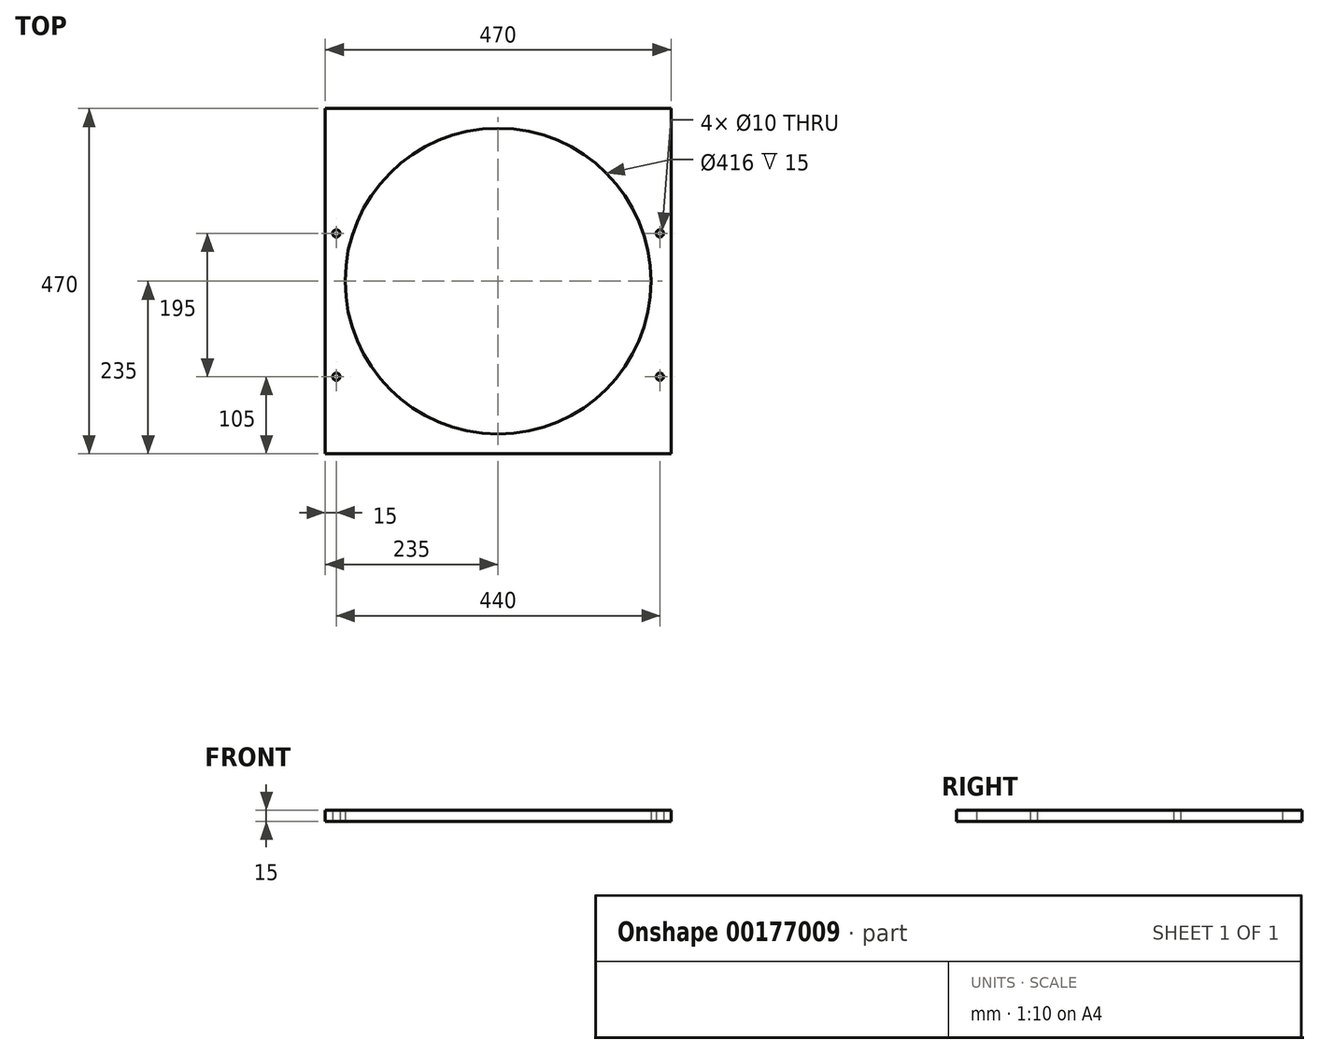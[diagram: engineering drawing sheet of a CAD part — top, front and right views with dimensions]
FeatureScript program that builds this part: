
annotation { "Feature Type Name" : "Feature", "Feature Type Description" : "" }
export const myFeature = defineFeature(function(context is Context, id is Id, definition is map)
    precondition{}
    {
        {
            var Q0;
            Q0=qCreatedBy(makeId("Top.planeOp"),FACE);
            var sketch = newSketch(context, id + "F0", { "sketchPlane" : qUnion([Q0])});
            skLineSegment(sketch, "E0.bottom", {"start": v(-235, 235) * mm, "end": v(235, 235) * mm});
            skLineSegment(sketch, "E0.top", {"start": v(-235, -235) * mm, "end": v(235, -235) * mm});
            skLineSegment(sketch, "E0.left", {"start": v(-235, 235) * mm, "end": v(-235, -235) * mm});
            skLineSegment(sketch, "E0.right", {"start": v(235, 235) * mm, "end": v(235, -235) * mm});
            skPoint(sketch, "E0.middle", {"position": v(0, 0) * mm});
            skCircle(sketch, "E1", {"center": v(0, 0) * mm, "radius": 208 * mm});
            skLineSegment(sketch, "E2", {"start": v(-220, 235) * mm, "end": v(-220, -235) * mm, "construction": true});
            skLineSegment(sketch, "E3", {"start": v(220, 235) * mm, "end": v(220, -235) * mm, "construction": true});
            skCircle(sketch, "E4", {"center": v(220, 65) * mm, "radius": 5 * mm});
            skCircle(sketch, "E5", {"center": v(220, -130) * mm, "radius": 5 * mm});
            skCircle(sketch, "E6", {"center": v(-220, 65) * mm, "radius": 5 * mm});
            skCircle(sketch, "E7", {"center": v(-220, -130) * mm, "radius": 5 * mm});
            skSolve(sketch);
        }
        {
            var Q0;
            Q0=makeQuery(id+"F0.imprint","IMPRINT",FACE,{"disambiguationData":[TD([[makeQuery(id+"F0.imprint","IMPRINT",EDGE,{"derivedFrom":sQuery(id+"F0.wireOp",EDGE,"E0.bottom")}),-1.0]])]});
            extrude(context, id + "F1", {"entities" : qUnion([Q0]), "depth" : 15 * mm});
        }
    });
